# Revit family: 63_UN_FreeStanding_PTA 3000LM_Norton
name_source: partatom
category: Lighting Fixtures
units: mm (PartAtom-declared; Revit-internal decimal feet)

## family parameters
Always vertical = Yes
Cut with Voids When Loaded = Yes
Light Source = No
OmniClass Number = 23.80.70.11.14.11
OmniClass Title = Downlights
Part Type = Normal
Room Calculation Point = Yes
Round Connector Dimension = Use Diameter
Shared = No
Work Plane-Based = No

## types (1)
- PTA LED 84 3000LM
    Apparent Load = 25 VA
    Assembly Code = 63.0
    Calc_Symbol_Length = 610 mm  [stored 2.00131 ft]
    Calc_Symbol_Width = 160 mm  [stored 0.524934 ft]
    Description = IP66 / IK10
    Housing_Material = Anthracite
    IfcExportAs = IfcLightFixtureType
    IfcExportType = USERDEFINED
    Lamp = LED
    Luminous Flux (lm) = 3160 lm
    Manufacturer = Norton
    Model = PTA
    URL = https://www.norton.nl
    Voltage = 230 V
    Wattage Comments = 25W
    Weight = 3,3kg

note: [stored X ft] marks values corroborated as IEEE doubles in the binary element streams (Revit-internal decimal feet)

## geometry (parser evidence)
native form markers: Sweep x12
no freeform markers — native parametric forms only
